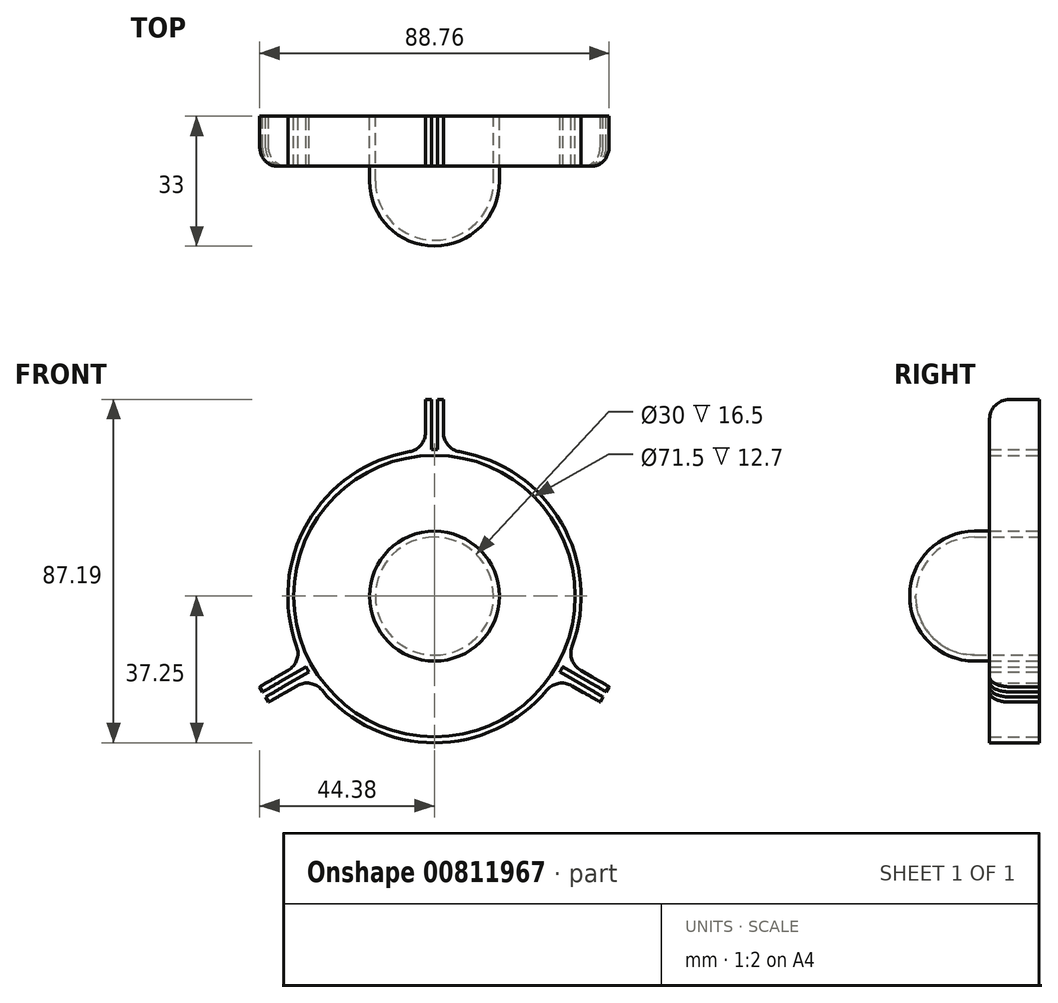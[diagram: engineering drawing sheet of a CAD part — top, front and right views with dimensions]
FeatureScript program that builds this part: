
annotation { "Feature Type Name" : "Feature", "Feature Type Description" : "" }
export const myFeature = defineFeature(function(context is Context, id is Id, definition is map)
    precondition{}
    {
        {
            var Q0;
            Q0=qCreatedBy(makeId("Front.planeOp"),FACE);
            var sketch = newSketch(context, id + "F0", { "sketchPlane" : qUnion([Q0])});
            skCircle(sketch, "E0", {"center": v(0, 0) * mm, "radius": 35.75 * mm});
            skArc(sketch, "E1.0", {"start": v(-2.25, 37.18) * mm, "mid": v(-32.26, 18.63) * mm, "end": v(-33.33, -16.64) * mm});
            skLineSegment(sketch, "E2", {"start": v(0, 0) * mm, "end": v(0, 50.09) * mm, "construction": true});
            skLineSegment(sketch, "E3.0", {"start": v(0.75, 37.24) * mm, "end": v(0.75, 49.94) * mm});
            skLineSegment(sketch, "E4.1", {"start": v(-0.75, 37.24) * mm, "end": v(-0.75, 49.94) * mm});
            skLineSegment(sketch, "E5.0", {"start": v(2.25, 37.18) * mm, "end": v(2.25, 49.94) * mm});
            skLineSegment(sketch, "E5.2", {"start": v(-2.25, 37.18) * mm, "end": v(-2.25, 49.94) * mm});
            skLineSegment(sketch, "E6", {"start": v(-2.25, 49.94) * mm, "end": v(-0.75, 49.94) * mm});
            skLineSegment(sketch, "E7.trimOffspring", {"start": v(0.75, 49.94) * mm, "end": v(2.25, 49.94) * mm});
            skArc(sketch, "E8.trimOffspring", {"start": v(0.75, 37.24) * mm, "mid": v(0, 37.25) * mm, "end": v(-0.75, 37.24) * mm});
            skLineSegment(sketch, "E9.1.0", {"start": v(-31.08, -20.54) * mm, "end": v(-42.13, -26.92) * mm});
            skLineSegment(sketch, "E9.1.1", {"start": v(-42.13, -26.92) * mm, "end": v(-42.88, -25.62) * mm});
            skLineSegment(sketch, "E9.1.2", {"start": v(-31.88, -19.27) * mm, "end": v(-42.88, -25.62) * mm});
            skLineSegment(sketch, "E9.1.3", {"start": v(-32.63, -17.97) * mm, "end": v(-43.63, -24.32) * mm});
            skLineSegment(sketch, "E9.1.4", {"start": v(-43.63, -24.32) * mm, "end": v(-44.38, -23.02) * mm});
            skLineSegment(sketch, "E9.1.5", {"start": v(-33.33, -16.64) * mm, "end": v(-44.38, -23.02) * mm});
            skLineSegment(sketch, "E9.2.0", {"start": v(33.33, -16.64) * mm, "end": v(44.38, -23.02) * mm});
            skLineSegment(sketch, "E9.2.1", {"start": v(44.38, -23.02) * mm, "end": v(43.63, -24.32) * mm});
            skLineSegment(sketch, "E9.2.2", {"start": v(32.63, -17.97) * mm, "end": v(43.63, -24.32) * mm});
            skLineSegment(sketch, "E9.2.3", {"start": v(31.88, -19.27) * mm, "end": v(42.88, -25.62) * mm});
            skLineSegment(sketch, "E9.2.4", {"start": v(42.88, -25.62) * mm, "end": v(42.13, -26.92) * mm});
            skLineSegment(sketch, "E9.2.5", {"start": v(31.08, -20.54) * mm, "end": v(42.13, -26.92) * mm});
            skArc(sketch, "E10.trimOffspring", {"start": v(33.33, -16.64) * mm, "mid": v(32.26, 18.62) * mm, "end": v(2.25, 37.18) * mm});
            skArc(sketch, "E11.trimOffspring", {"start": v(31.88, -19.27) * mm, "mid": v(32.26, -18.63) * mm, "end": v(32.63, -17.97) * mm});
            skArc(sketch, "E12.trimOffspring", {"start": v(-31.08, -20.54) * mm, "mid": v(0, -37.25) * mm, "end": v(31.08, -20.54) * mm});
            skArc(sketch, "E13.trimOffspring", {"start": v(-32.63, -17.97) * mm, "mid": v(-32.26, -18.62) * mm, "end": v(-31.88, -19.27) * mm});
            skSolve(sketch);
        }
        {
            var Q0;
            Q0 = qSketchRegion(id + "F0", true);
            extrude(context, id + "F1", {"entities" : qUnion([Q0]), "depth" : 12.7 * mm, "offsetDistance" : 25 * mm});
        }
        {
            var Q0;
            Q0=makeQuery(id+"F1.opExtrude","SWEPT_EDGE",EDGE,{"disambiguationData":[OSD([sQuery(id+"F0.wireOp",EDGE,"E9.2.5"),sQuery(id+"F0.wireOp",EDGE,"E12.trimOffspring")])]});
            var Q1;
            Q1=makeQuery(id+"F1.opExtrude","SWEPT_EDGE",EDGE,{"disambiguationData":[OSD([sQuery(id+"F0.wireOp",EDGE,"E9.1.0"),sQuery(id+"F0.wireOp",EDGE,"E12.trimOffspring")])]});
            var Q2;
            Q2=makeQuery(id+"F1.opExtrude","SWEPT_EDGE",EDGE,{"disambiguationData":[OSD([sQuery(id+"F0.wireOp",EDGE,"E1.0"),sQuery(id+"F0.wireOp",EDGE,"E9.1.5")])]});
            var Q3;
            Q3=makeQuery(id+"F1.opExtrude","SWEPT_EDGE",EDGE,{"disambiguationData":[OSD([sQuery(id+"F0.wireOp",EDGE,"E1.0"),sQuery(id+"F0.wireOp",EDGE,"E5.2")])]});
            var Q4;
            Q4=makeQuery(id+"F1.opExtrude","SWEPT_EDGE",EDGE,{"disambiguationData":[OSD([sQuery(id+"F0.wireOp",EDGE,"E5.0"),sQuery(id+"F0.wireOp",EDGE,"E10.trimOffspring")])]});
            var Q5;
            Q5=makeQuery(id+"F1.opExtrude","SWEPT_EDGE",EDGE,{"disambiguationData":[OSD([sQuery(id+"F0.wireOp",EDGE,"E9.2.0"),sQuery(id+"F0.wireOp",EDGE,"E10.trimOffspring")])]});
            fillet(context, id + "F2", {"entities" : qUnion([Q0, Q1, Q2, Q3, Q4, Q5]), "radius" : 5 * mm, "tangentPropagation" : true, "allowEdgeOverflow" : false});
        }
        {
            var Q0;
            Q0=makeQuery(id+"F1.opExtrude","CAP_EDGE",EDGE,{"disambiguationData":[OSD([sQuery(id+"F0.wireOp",EDGE,"E9.2.1")])],"isStart":false});
            var Q1;
            Q1=makeQuery(id+"F1.opExtrude","CAP_EDGE",EDGE,{"disambiguationData":[OSD([sQuery(id+"F0.wireOp",EDGE,"E9.2.4")])],"isStart":false});
            var Q2;
            Q2=makeQuery(id+"F1.opExtrude","CAP_EDGE",EDGE,{"disambiguationData":[OSD([sQuery(id+"F0.wireOp",EDGE,"E9.1.1")])],"isStart":false});
            var Q3;
            Q3=makeQuery(id+"F1.opExtrude","CAP_EDGE",EDGE,{"disambiguationData":[OSD([sQuery(id+"F0.wireOp",EDGE,"E9.1.4")])],"isStart":false});
            var Q4;
            Q4=makeQuery(id+"F1.opExtrude","CAP_EDGE",EDGE,{"disambiguationData":[OSD([sQuery(id+"F0.wireOp",EDGE,"E6")])],"isStart":false});
            var Q5;
            Q5=makeQuery(id+"F1.opExtrude","CAP_EDGE",EDGE,{"disambiguationData":[OSD([sQuery(id+"F0.wireOp",EDGE,"E7.trimOffspring")])],"isStart":false});
            fillet(context, id + "F3", {"entities" : qUnion([Q0, Q1, Q2, Q3, Q4, Q5]), "radius" : 5 * mm, "tangentPropagation" : true, "allowEdgeOverflow" : false});
        }
        {
            var Q0;
            Q0=qCreatedBy(makeId("Front.planeOp"),FACE);
            var sketch = newSketch(context, id + "F4", { "sketchPlane" : qUnion([Q0])});
            skCircle(sketch, "E14", {"center": v(0, 0) * mm, "radius": 16.5 * mm});
            skSolve(sketch);
        }
        {
            var Q0;
            Q0 = qSketchRegion(id + "F4", true);
            extrude(context, id + "F5", {"entities" : qUnion([Q0]), "depth" : 33 * mm, "offsetDistance" : 25 * mm});
        }
        {
            var Q0;
            Q0=makeQuery(id+"F5.opExtrude","CAP_EDGE",EDGE,{"disambiguationData":[OSD([sQuery(id+"F4.wireOp",EDGE,"E14")])],"isStart":false});
            fillet(context, id + "F6", {"entities" : qUnion([Q0]), "radius" : 16.5 * mm, "tangentPropagation" : true, "allowEdgeOverflow" : false});
        }
        {
            var Q0;
            Q0=makeQuery(id+"F5.opExtrude","CAP_FACE",FACE,{"disambiguationData":[OSD([sQuery(id+"F4.wireOp",EDGE,"E14")])],"isStart":true});
            shell(context, id + "F7", {"entities" : qUnion([Q0]), "thickness" : 1.5 * mm});
        }
    });
